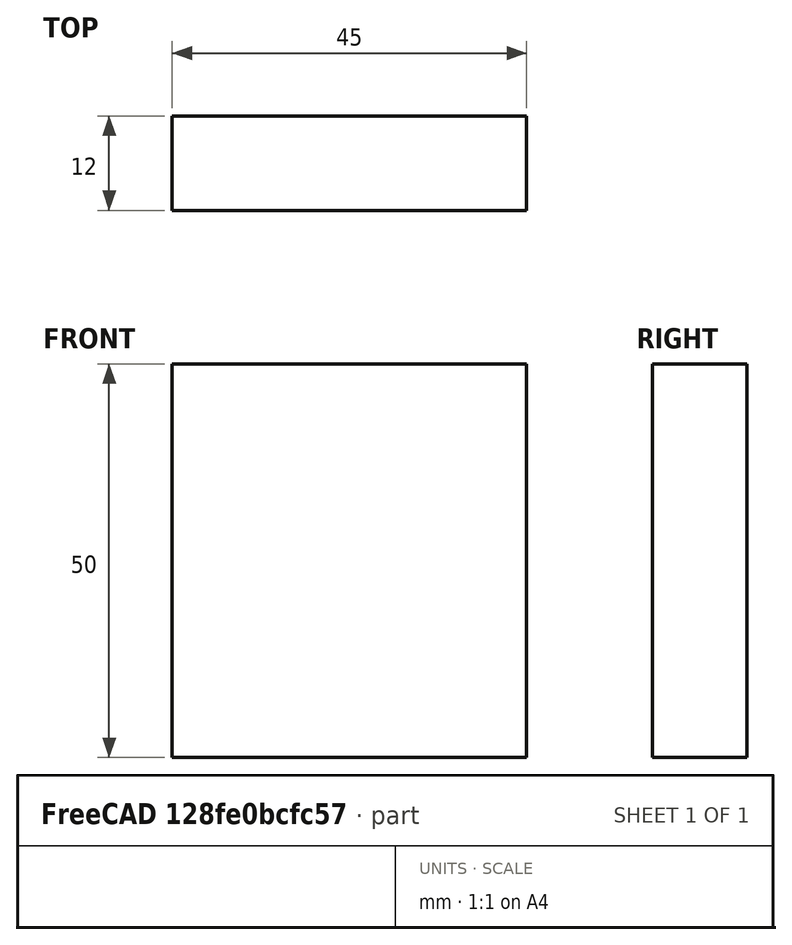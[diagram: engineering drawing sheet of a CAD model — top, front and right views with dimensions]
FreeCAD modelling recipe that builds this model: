
FCSTD DOCUMENT  (FreeCAD 0.15R4671 (Git))
Label: Flat Bar 45x12 EN10058 S235JR
License: All rights reserved
LicenseURL: http://en.wikipedia.org/wiki/All_rights_reserved
objects: Sketcher::SketchObject×1, Part::Extrusion×1
note: 2 computed .brp shape members not serialized (recipe doc carries the construction recipe); baked Part::Feature solids carry a one-line shape summary decoded from their .brp

FEATURE [Sketcher::SketchObject] Sketch
  sketch-geometry (4):
    g0: LineSegment StartX=-22.5 StartY=-6 StartZ=0 EndX=22.5 EndY=-6 EndZ=0
    g1: LineSegment StartX=22.5 StartY=-6 StartZ=0 EndX=22.5 EndY=6 EndZ=0
    g2: LineSegment StartX=22.5 StartY=6 StartZ=0 EndX=-22.5 EndY=6 EndZ=0
    g3: LineSegment StartX=-22.5 StartY=6 StartZ=0 EndX=-22.5 EndY=-6 EndZ=0
  constraints (12):
    c: Coincident(g0,g1)
    c: Coincident(g1,g2)
    c: Coincident(g2,g3)
    c: Coincident(g3,g0)
    c: Horizontal(g0)
    c: Horizontal(g2)
    c: Vertical(g1)
    c: Vertical(g3)
    c: Symmetric(g1,g2,g-2)
    c: Symmetric(g0,g1,g-1)
    c: DistanceY(g1) = 12
    c: DistanceX(g0) = 45
FEATURE [Part::Extrusion] Extrude  label="Flat Bar 45x12 EN10058 S235JR"
  Base = -> Sketch
  Dir = (0,0,50)
  Solid = true
